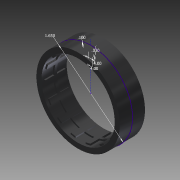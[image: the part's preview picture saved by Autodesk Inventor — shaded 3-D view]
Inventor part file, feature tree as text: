
AUTODESK INVENTOR PART (.ipt)
format: ipt  version: 2015 (Build 190159000, 159)  size: 215,040 bytes
history: native  units: in
note: dims shown in document units (in); Inventor stores cm internally (conversion verified against a paired STEP export)
features: extrude x3, sketch x2, pattern_circular x1, plane x1
ambient origin geometry x8: Origin, YZ Plane, XZ Plane, XY Plane, X Axis, Y Axis, Z Axis, Center Point
bodies: Solid1 (feature_tree)
feature tree (7):
  sketch  "Sketch1"  dims[d0=1.65in d1=0.1in]
  extrude  "Extrusion1"  Depth=0.1in
  extrude  "Extrusion2"  Depth=0.05in
  pattern_circular  "Circular Pattern1"  [2 undecoded]
  plane  "Work Plane1"
  extrude  "Extrusion3"  Depth=0.05in
  sketch  "Sketch2"  dims[d2=0.03in d3=0.0275in d4=0.0275in d5=0.0275in d6=0.5in d7=0.0in d8=0.4in d9=0.0in d10=5.9055in d11=360.0deg d13=0.05in d14=0.0in]
note: 2 required parameter values undecoded (feature->parameter linkage not recoverable at this tier; creation-order binding heuristic only, values carry confidence <= 0.55)
